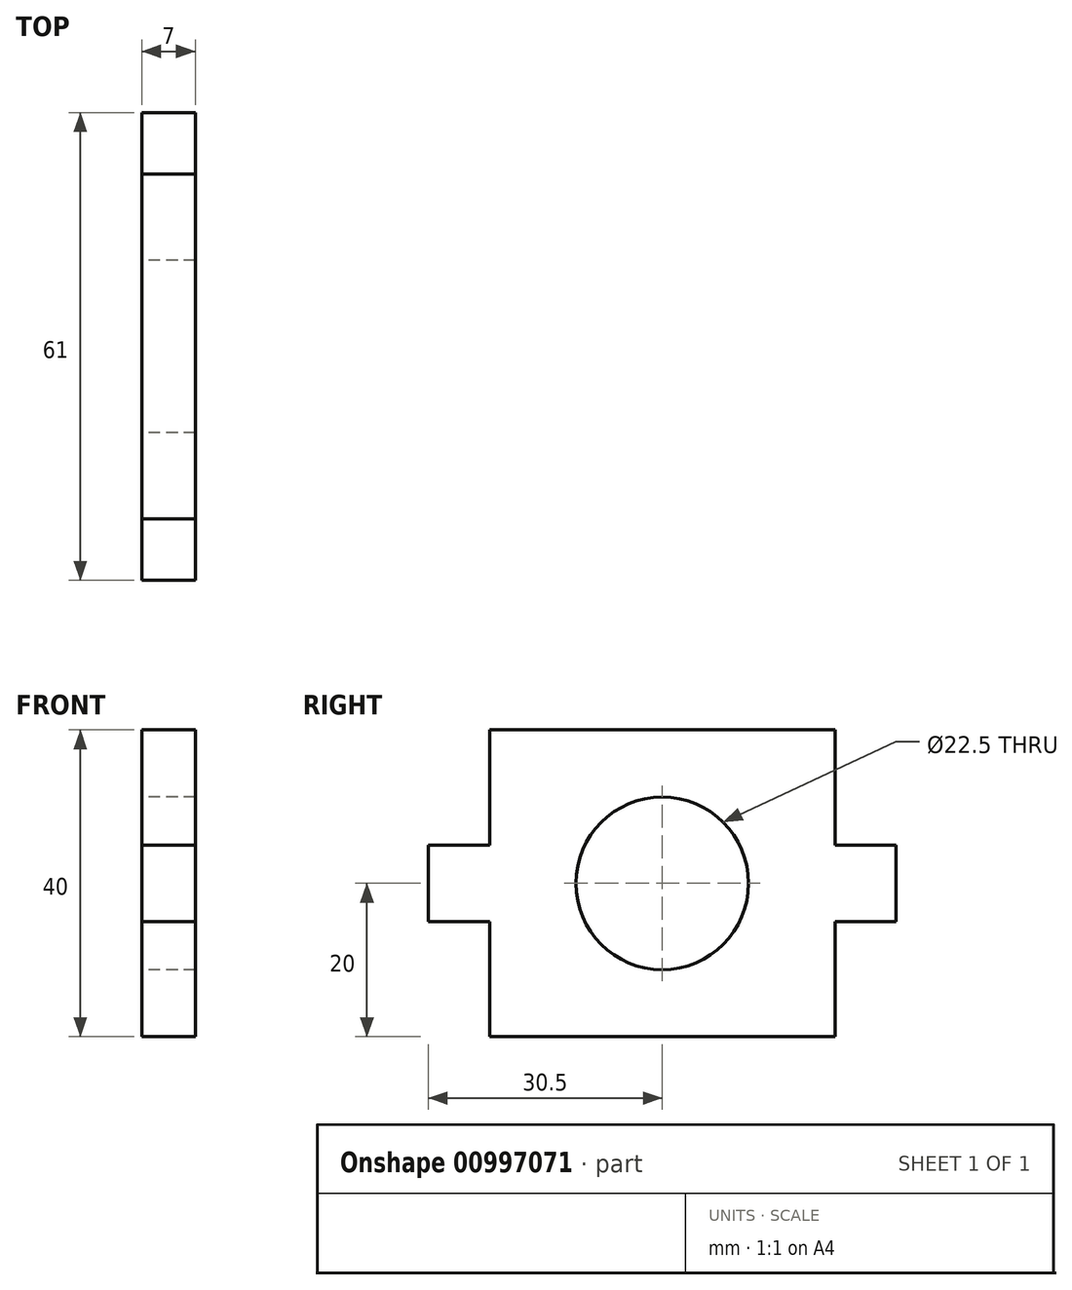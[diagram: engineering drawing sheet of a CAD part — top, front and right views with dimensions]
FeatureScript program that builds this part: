
annotation { "Feature Type Name" : "Feature", "Feature Type Description" : "" }
export const myFeature = defineFeature(function(context is Context, id is Id, definition is map)
    precondition{}
    {
        {
            var Q0;
            Q0=qCreatedBy(makeId("Right.planeOp"),FACE);
            var sketch = newSketch(context, id + "F0", { "sketchPlane" : qUnion([Q0])});
            skLineSegment(sketch, "E0.bottom", {"start": v(0, 0) * mm, "end": v(45, 0) * mm});
            skLineSegment(sketch, "E0.top", {"start": v(0, 40) * mm, "end": v(45, 40) * mm});
            skLineSegment(sketch, "E0.left", {"start": v(0, 0) * mm, "end": v(0, 15) * mm});
            skLineSegment(sketch, "E0.right", {"start": v(45, 0) * mm, "end": v(45, 15) * mm});
            skLineSegment(sketch, "E1.bottom", {"start": v(0, 25) * mm, "end": v(-8, 25) * mm});
            skLineSegment(sketch, "E1.top", {"start": v(0, 15) * mm, "end": v(-8, 15) * mm});
            skLineSegment(sketch, "E1.right", {"start": v(-8, 25) * mm, "end": v(-8, 15) * mm});
            skLineSegment(sketch, "E2.bottom", {"start": v(45, 25) * mm, "end": v(53, 25) * mm});
            skLineSegment(sketch, "E2.top", {"start": v(45, 15) * mm, "end": v(53, 15) * mm});
            skLineSegment(sketch, "E2.right", {"start": v(53, 25) * mm, "end": v(53, 15) * mm});
            skLineSegment(sketch, "E3.trimOffspring", {"start": v(0, 25) * mm, "end": v(0, 40) * mm});
            skLineSegment(sketch, "E4.trimOffspring", {"start": v(45, 25) * mm, "end": v(45, 40) * mm});
            skCircle(sketch, "E5", {"center": v(22.5, 20) * mm, "radius": 11.25 * mm});
            skPoint(sketch, "E6", {"position": v(-8, 20) * mm});
            skPoint(sketch, "E7", {"position": v(22.5, 40) * mm});
            skSolve(sketch);
        }
        {
            var Q0;
            Q0 = qSketchRegion(id + "F0", true);
            extrude(context, id + "F1", {"entities" : qUnion([Q0]), "depth" : 7 * mm, "offsetDistance" : 25 * mm});
        }
    });
